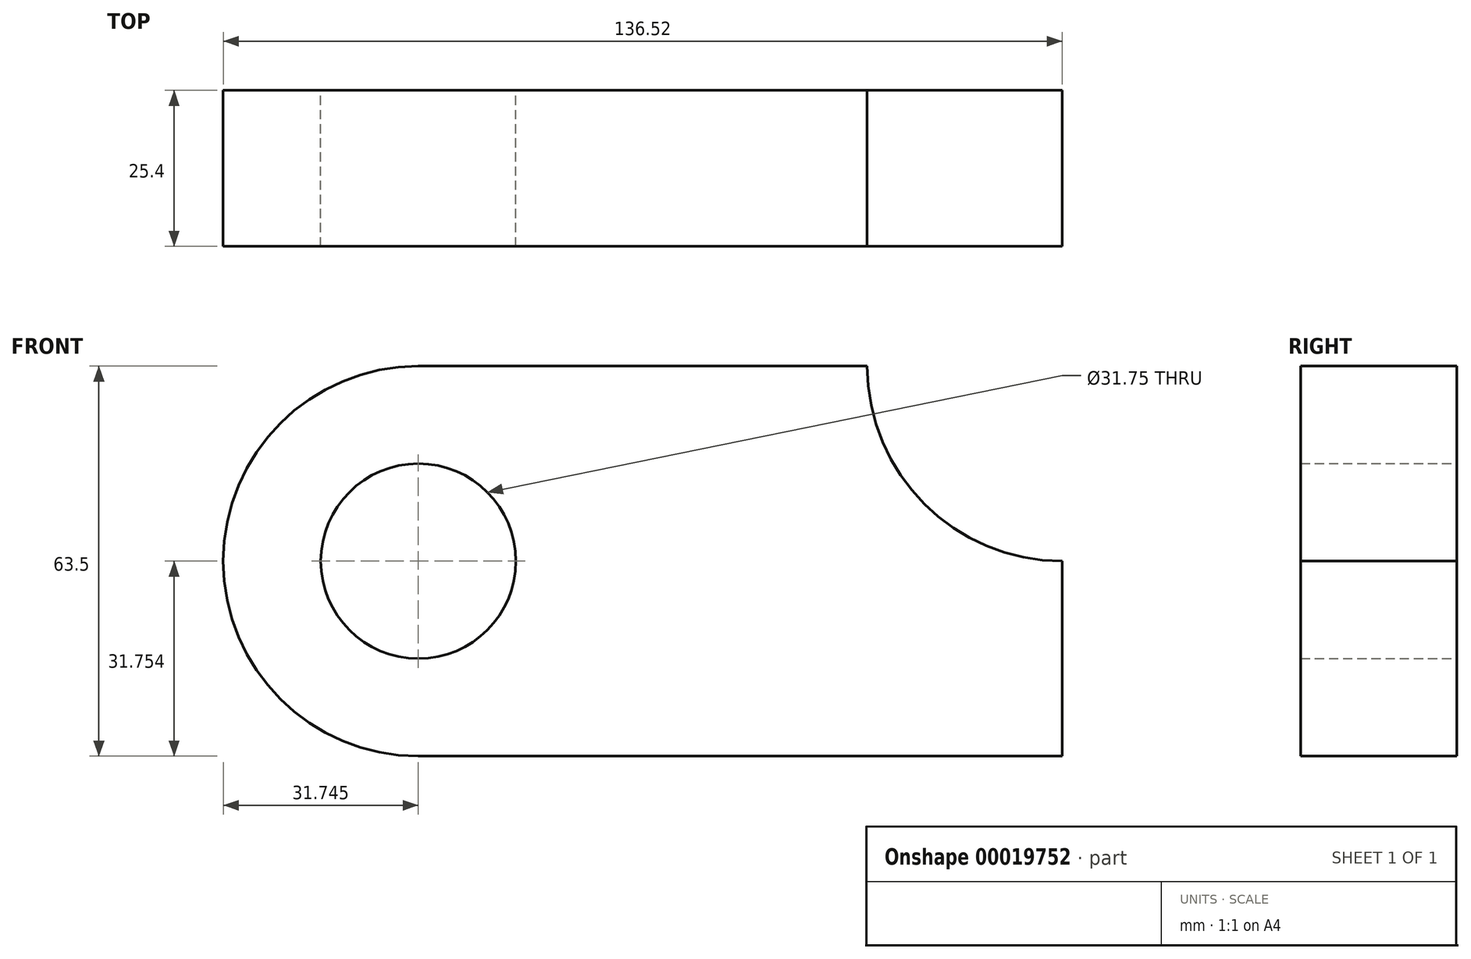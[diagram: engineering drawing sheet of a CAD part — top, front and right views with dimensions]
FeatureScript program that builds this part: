
annotation { "Feature Type Name" : "Feature", "Feature Type Description" : "" }
export const myFeature = defineFeature(function(context is Context, id is Id, definition is map)
    precondition{}
    {
        {
            var Q0;
            Q0=qCreatedBy(makeId("Front.planeOp"),FACE);
            var sketch = newSketch(context, id + "F0", { "sketchPlane" : qUnion([Q0])});
            skLineSegment(sketch, "E0.bottom", {"start": v(-53.17, 35.41) * mm, "end": v(19.85, 35.41) * mm});
            skLineSegment(sketch, "E0.top", {"start": v(-53.17, -28.09) * mm, "end": v(51.6, -28.09) * mm});
            skLineSegment(sketch, "E0.left", {"start": v(-53.17, 35.41) * mm, "end": v(-53.17, -28.09) * mm});
            skLineSegment(sketch, "E0.right", {"start": v(51.6, 3.66) * mm, "end": v(51.6, -28.09) * mm});
            skArc(sketch, "E1", {"start": v(-53.17, 35.41) * mm, "mid": v(-84.92, 3.66) * mm, "end": v(-53.17, -28.09) * mm});
            skCircle(sketch, "E2", {"center": v(-53.17, 3.66) * mm, "radius": 15.88 * mm});
            skArc(sketch, "E3", {"start": v(19.85, 35.41) * mm, "mid": v(29.15, 12.96) * mm, "end": v(51.6, 3.66) * mm});
            skSolve(sketch);
        }
        {
            var Q0;
            {var subQ6=sQuery(id+"F0.wireOp",EDGE,"E0.bottom");Q0=makeQuery(id+"F0.imprint","IMPRINT",FACE,{"disambiguationData":[TD([[makeQuery(id+"F0.imprint","IMPRINT",EDGE,{"derivedFrom":subQ6}),-1.0]])]});}
            var Q1;
            {var subQ4=sQuery(id+"F0.wireOp",EDGE,"E1");Q1=makeQuery(id+"F0.imprint","IMPRINT",FACE,{"disambiguationData":[TD([[makeQuery(id+"F0.imprint","IMPRINT",EDGE,{"derivedFrom":subQ4}),1.0]])]});}
            extrude(context, id + "F1", {"entities" : qUnion([Q0, Q1]), "depth" : 25.4 * mm});
        }
    });
